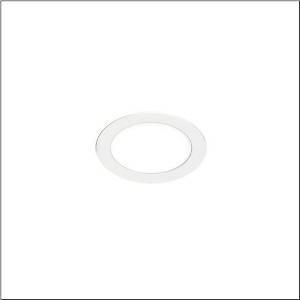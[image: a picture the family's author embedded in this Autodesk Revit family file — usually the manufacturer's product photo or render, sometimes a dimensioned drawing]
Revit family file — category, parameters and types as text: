
# Revit family: lunis_41_flat_51dr10mdhbb
name_source: partatom
category: Lighting Fixtures
units: mm (PartAtom-declared; Revit-internal decimal feet)

## family parameters
Cut with Voids When Loaded = No
Host = Face
Light Source = No
Part Type = Normal
Room Calculation Point = No
Round Connector Dimension = Use Diameter
Shared = No

## types (1)
- --- (1 x LED, 1600 lm, 12.5 W, 6500K)
    Apparent Load = 13 VA
    CIE Flux Codes = 49 80 96 100 100
    Color Rendering = 80
    Color Temperature = 6500K
    Default Elevation = 1800 mm
    Description = Lunis 41 Flat, downlight, light emission: direct distribution, LED rated luminous flux: 1.580lm, light colour: 840/865, mains connection: 230V, AC, 50/60Hz, housing, round, of aluminium, coated, traffic white (RAL 9016), diameter: 170mm, protection rating (complete): IP20, protection rating (on room side): IP44, insulation class (complete): insulation class II (safety insulation), certification: CE, permissible ambient temperature for indoor applications: -20..+40°C, packaging unit: 1 piece
    Height = 0 mm  [stored 0 ft]
    Lamp = 1 x LED
    Lamp Light Flux = 1600 lm
    Lamp Power = 12.5 W
    Lamp count = 1
    Length = 170 mm  [stored 0.557743 ft]
    Luminous efficacy = 128 lm/W
    Manufacturer = Siteco
    ModVariant = No
    Model = 51DR10MDHBB
    Mounting Place = Ceiling
    Mounting Type = Recessed
    Number of Poles = 1
    OnlyDefault = Yes
    Power Factor = 1
    Product Name = Lunis 41 Flat
    Product group = downlight
    ProductGroupID = 401
    Protection Class = Protection class II
    Protection Degree = IP 20
    RLX_Detail_Level = 1
    RLX_Emergency_Light_Flux = 0 lm
    RLX_Emergency_Type = 0
    RLX_Emergency_Type_DB = No
    RlxData = <blob elided: 9765 chars, md5=2b9d93c9>
    Socket = socket
    Standby Power = 0 W
    System Light Flux = 1600 lm
    System Power = 13 W
    Type Comments = individual setting: colour temperature 6500K
    Type Image = l_1340921.jpg
    URL = http://relux.com
    VarID = @adj_020037
    Voltage = 0 V
    Weight = 0.00 kg
    Width = 0 mm  [stored 0 ft]

note: [stored X ft] marks values corroborated as IEEE doubles in the binary element streams (Revit-internal decimal feet)

## geometry (parser evidence)
native form markers: Sweep x10
no freeform markers — native parametric forms only
